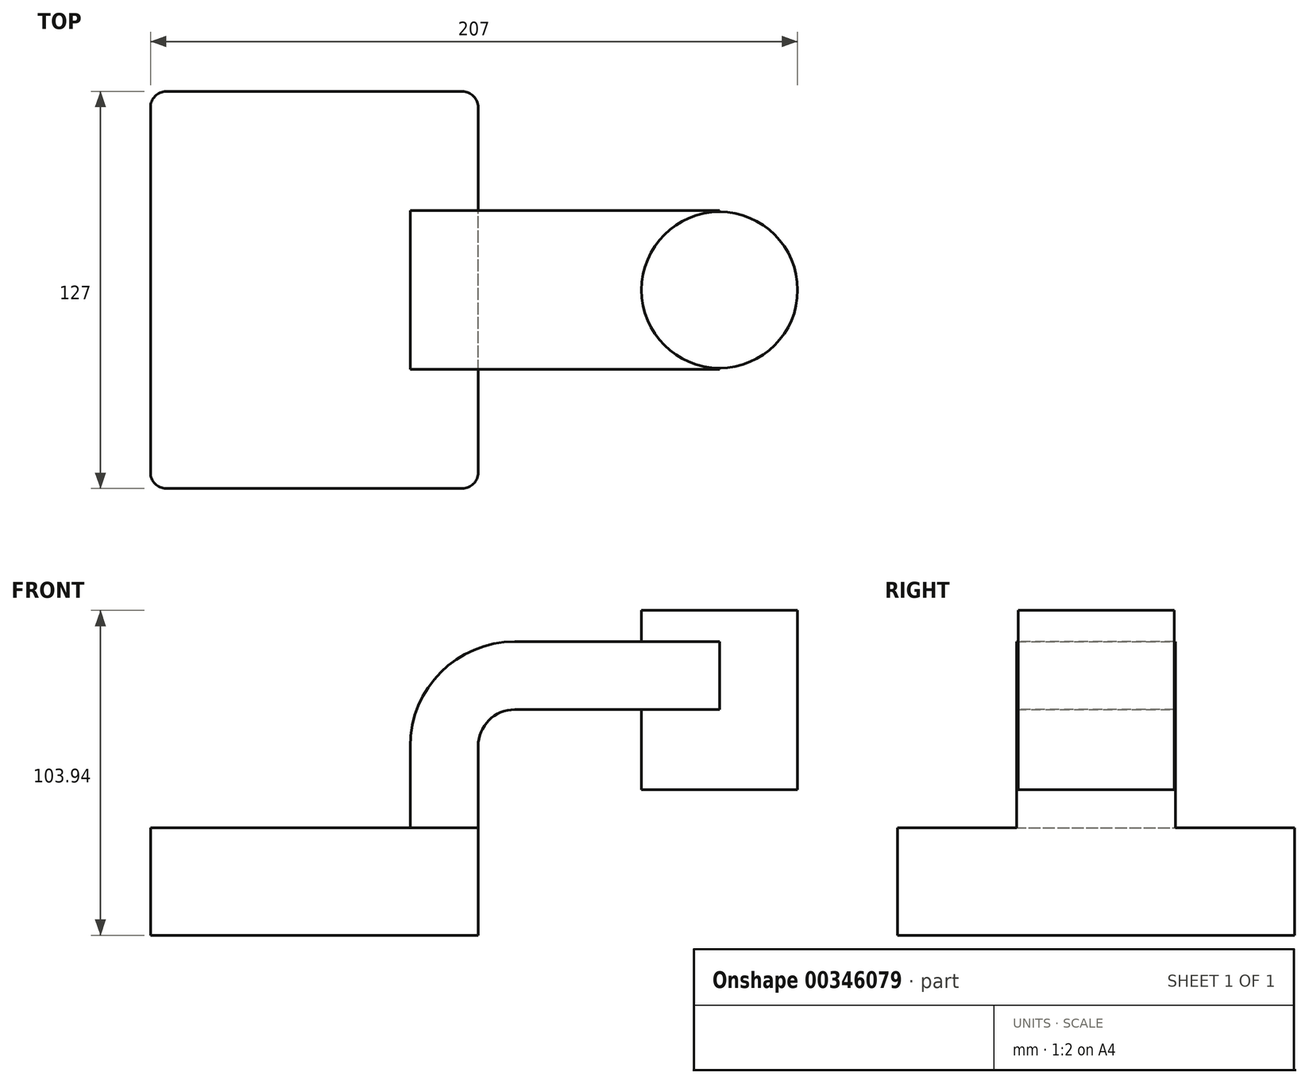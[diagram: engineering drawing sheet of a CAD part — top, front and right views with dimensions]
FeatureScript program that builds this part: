
annotation { "Feature Type Name" : "Feature", "Feature Type Description" : "" }
export const myFeature = defineFeature(function(context is Context, id is Id, definition is map)
    precondition{}
    {
        {
            var Q0;
            Q0=qCreatedBy(makeId("Front.planeOp"),FACE);
            var sketch = newSketch(context, id + "F0", { "sketchPlane" : qUnion([Q0])});
            skLineSegment(sketch, "E0.bottom", {"start": v(52.4, 17.18) * mm, "end": v(-52.4, 17.18) * mm});
            skLineSegment(sketch, "E0.top", {"start": v(52.4, -17.18) * mm, "end": v(-52.4, -17.18) * mm});
            skLineSegment(sketch, "E0.left", {"start": v(52.4, 17.18) * mm, "end": v(52.4, -17.18) * mm});
            skLineSegment(sketch, "E0.right", {"start": v(-52.4, 17.18) * mm, "end": v(-52.4, -17.18) * mm});
            skPoint(sketch, "E0.middle", {"position": v(0, 0) * mm});
            skLineSegment(sketch, "E1.bottom", {"start": v(154.6, 86.76) * mm, "end": v(104.15, 86.76) * mm});
            skLineSegment(sketch, "E1.top", {"start": v(154.6, 29.35) * mm, "end": v(104.15, 29.35) * mm});
            skLineSegment(sketch, "E1.left", {"start": v(154.6, 86.76) * mm, "end": v(154.6, 29.35) * mm});
            skLineSegment(sketch, "E1.right", {"start": v(104.15, 86.76) * mm, "end": v(104.15, 29.35) * mm});
            skPoint(sketch, "E1.middle", {"position": v(129.37, 58.06) * mm});
            skLineSegment(sketch, "E2", {"start": v(52.4, 17.18) * mm, "end": v(52.4, 43.27) * mm});
            skArc(sketch, "E3", {"start": v(52.4, 43.27) * mm, "mid": v(55.84, 51.57) * mm, "end": v(64.14, 55.01) * mm});
            skLineSegment(sketch, "E4", {"start": v(64.14, 55.01) * mm, "end": v(129.62, 55.01) * mm});
            skLineSegment(sketch, "E5.0", {"start": v(64.14, 76.75) * mm, "end": v(129.62, 76.75) * mm});
            skArc(sketch, "E5.1", {"start": v(30.66, 43.27) * mm, "mid": v(40.47, 66.95) * mm, "end": v(64.14, 76.75) * mm});
            skLineSegment(sketch, "E5.2", {"start": v(30.66, 17.18) * mm, "end": v(30.66, 43.27) * mm});
            skFitSpline(sketch, "E6", {"points": [v(-52.4, 17.18) * mm, v(64.14, 76.75) * mm], "startDerivative": vector(2.6, 110.9) * mm, "endDerivative": vector(118.72, -2.6) * mm});
            skLineSegment(sketch, "E7", {"start": v(129.62, 76.75) * mm, "end": v(129.62, 55.01) * mm});
            skLineSegment(sketch, "E8", {"start": v(129.62, 86.76) * mm, "end": v(129.62, 29.35) * mm});
            skPoint(sketch, "E8.startSnap0", {"position": v(129.37, 86.76) * mm});
            skSolve(sketch);
        }
        {
            var Q0;
            Q0=makeQuery(id+"F0.imprint","IMPRINT",FACE,{"disambiguationData":[TD([[makeQuery(id+"F0.imprint","IMPRINT",EDGE,{"derivedFrom":sQuery(id+"F0.wireOp",EDGE,"E0.top")}),-1.0]])]});
            extrude(context, id + "F1", {"entities" : qUnion([Q0]), "endBound" : BoundingType.SYMMETRIC, "depth" : 127 * mm, "offsetDistance" : 25.4 * mm});
        }
        {
            var Q0;
            {var subQ1=sQuery(id+"F0.wireOp",EDGE,"E2");Q0=makeQuery(id+"F0.imprint","IMPRINT",FACE,{"disambiguationData":[TD([[makeQuery(id+"F0.imprint","IMPRINT",EDGE,{"derivedFrom":subQ1}),1.0]])]});}
            var Q1;
            {var subQ5=sQuery(id+"F0.wireOp",EDGE,"E7");Q1=makeQuery(id+"F0.imprint","IMPRINT",FACE,{"disambiguationData":[TD([[makeQuery(id+"F0.imprint","IMPRINT",EDGE,{"derivedFrom":subQ5}),-1.0]])]});}
            var Q2;
            {var subQ0=sQuery(id+"F0.wireOp",EDGE,"E5.0");var subQ1=sQuery(id+"F0.wireOp",EDGE,"E1.right");var subQ2=makeQuery(id+"F0.imprint","INTERSECT",VERTEX,{"derivedFrom":[subQ1,subQ0]});Q2=makeQuery(id+"F0.imprint","IMPRINT",FACE,{"disambiguationData":[TD([[makeQuery(id+"F0.imprint","IMPRINT",EDGE,{"disambiguationData":[TD([[subQ2,-1.0]])],"derivedFrom":subQ1}),1.0]])]});}
            extrude(context, id + "F2", {"entities" : qUnion([Q0, Q1, Q2]), "operationType" : NewBodyOperationType.ADD, "endBound" : BoundingType.SYMMETRIC, "depth" : 50.8 * mm, "offsetDistance" : 25.4 * mm});
        }
        {
            var Q0;
            Q0=makeQuery(id+"F0.imprint","IMPRINT",FACE,{"disambiguationData":[TD([[makeQuery(id+"F0.imprint","IMPRINT",EDGE,{"derivedFrom":sQuery(id+"F0.wireOp",EDGE,"E5.1")}),1.0]])]});
            extrude(context, id + "F3", {"entities" : qUnion([Q0]), "operationType" : NewBodyOperationType.ADD, "endBound" : BoundingType.SYMMETRIC, "depth" : 15.88 * mm, "offsetDistance" : 25.4 * mm});
        }
        {
            var Q0;
            {var subQ0=sQuery(id+"F0.wireOp",EDGE,"E1.left");Q0=makeQuery(id+"F0.imprint","IMPRINT",FACE,{"disambiguationData":[TD([[makeQuery(id+"F0.imprint","IMPRINT",EDGE,{"derivedFrom":subQ0}),-1.0]])]});}
            var Q1;
            Q1=sQuery(id+"F0.wireOp",EDGE,"E8");
            revolve(context, id + "F4", {"operationType" : NewBodyOperationType.ADD, "surfaceOperationType" : NewSurfaceOperationType.NEW, "entities" : qUnion([Q0]), "axis" : qUnion([Q1]), "revolveType" : RevolveType.FULL});
        }
        {
            var Q0;
            Q0=makeQuery(id+"F1.opExtrude","CAP_EDGE",EDGE,{"disambiguationData":[OSD([sQuery(id+"F0.wireOp",EDGE,"E0.right")])],"isStart":false});
            var Q1;
            Q1=makeQuery(id+"F1.opExtrude","CAP_EDGE",EDGE,{"disambiguationData":[OSD([sQuery(id+"F0.wireOp",EDGE,"E0.left")])],"isStart":false});
            var Q2;
            Q2=makeQuery(id+"F1.opExtrude","CAP_EDGE",EDGE,{"disambiguationData":[OSD([sQuery(id+"F0.wireOp",EDGE,"E0.left")])],"isStart":true});
            var Q3;
            Q3=makeQuery(id+"F1.opExtrude","CAP_EDGE",EDGE,{"disambiguationData":[OSD([sQuery(id+"F0.wireOp",EDGE,"E0.right")])],"isStart":true});
            fillet(context, id + "F5", {"entities" : qUnion([Q0, Q1, Q2, Q3]), "radius" : 5.08 * mm, "tangentPropagation" : true, "allowEdgeOverflow" : false});
        }
    });
